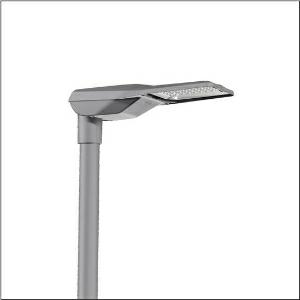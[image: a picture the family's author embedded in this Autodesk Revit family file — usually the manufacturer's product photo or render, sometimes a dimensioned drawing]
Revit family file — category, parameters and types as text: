
# Revit family: streetlight_sl_21_iq_mini___p0_8a_5xe2u31d08gb_8910
name_source: partatom
category: Lighting Fixtures
units: mm (PartAtom-declared; Revit-internal decimal feet)

## family parameters
Cut with Voids When Loaded = No
Host = Face
Light Source = No
Part Type = Normal
Room Calculation Point = No
Round Connector Dimension = Use Diameter
Shared = No

## types (1)
- --- (1 x LED, 5730 lm, 37.1 W, 3000K)
    Apparent Load = 37 VA
    CIE Flux Codes = 33 69 96 100 100
    Color Rendering = 70
    Color Temperature = 3000K
    Default Elevation = 1800 mm
    Description = Streetlight SL 21 iQ mini, mast luminaire, primary light control with lens, of PMMA, primary optical cover: cover, of toughened safety glass, transparent, light distribution: P0.8a, light emission: direct distribution, primary light characteristic: asymmetric, installation type: post-top, side-entry, LED, High Power LED, rated luminous flux: 5.730lm, luminous efficacy: 154lm/W, light colour: 730, colour temperature: 3000K, control gear: iQ-Comfort, control: pre-setting: linear dimming characteristic, Auto-Match, Temp-Guard, Lumen-Switch, Night-Set, Smart-Wire, Light-Fading, Desk-Remote (wireless, voltage-free reading and setting of iQ features in the workshop via application-optimized NFC function/RFID function), optimised constant luminous flux control (CLO 2.0), mains connection: 220..240V, AC, 50/60Hz, start of lifetime: 37W, end of service life: 39W, reduction: 18W, luminaire housing, of diecast aluminium, powder-coated, Siteco® metallic grey (DB 702S), corrosivity category C5 mid according to DIN EN ISO 12944, please order mast flange separately, inclination adjustable: 0°, 5°, 10°, 15°, sealing non-destructively replaceable, multi-level sealing system, length: 628mm, width: 235mm, height: 110mm, mast flange for spigot size: 42mm (side-entry): 5XC10008XM4, 60/48mm (side-entry/post-top): 5XC10108XM2, 76/60mm (side-entry/post-top): 5XC10108XM1, mounting height: 4..8m, protection rating (complete): IP66, insulation class (complete): insulation class II (safety insulation), certification: CE, ENEC, ENEC+, VDE, impact resistance: IK10, permissible operating ambient temperature for outdoor applications: -40..+50°C, standard-compliant lighting for roads and squares, packaging unit: 1 piece

Light Distribution: P0.8a
    Height = 110 mm
    Lamp = 1 x LED
    Lamp Light Flux = 5730 lm
    Lamp Power = 37.1 W
    Lamp count = 1
    Length = 625 mm
    Luminous efficacy = 154 lm/W
    Manufacturer = Siteco
    ModVariant = No
    Model = 5XE2U31D08GB
    Number of Poles = 1
    OnlyDefault = Yes
    Power Factor = 1
    Product Name = Streetlight SL 21 iQ mini | P0.8a
    Product group = mast luminaire | pylon top
    ProductGroupID = 6100
    Protection Class = Protection class II
    Protection Degree = IP 66
    RLX_Detail_Level = 1
    RLX_Emergency_Light_Flux = 0 lm
    RLX_Emergency_Type = 0
    RLX_Emergency_Type_DB = No
    RlxData = <blob elided: 26089 chars, md5=041ea3f1>
    Socket = socket
    Standby Power = 0 W
    System Light Flux = 5730 lm
    System Power = 37 W
    Type Comments = factory setting: luminous flux: 100 % | dim-lin: 254 | 385 mA
    Type Image = l_1003519.jpg
    URL = http://relux.com
    VarID = @adj_072738
    Voltage = 0 V
    Weight = 0.00 kg
    Width = 234 mm

## geometry (parser evidence)
native form markers: Blend x4, Sweep x10
no freeform markers — native parametric forms only
